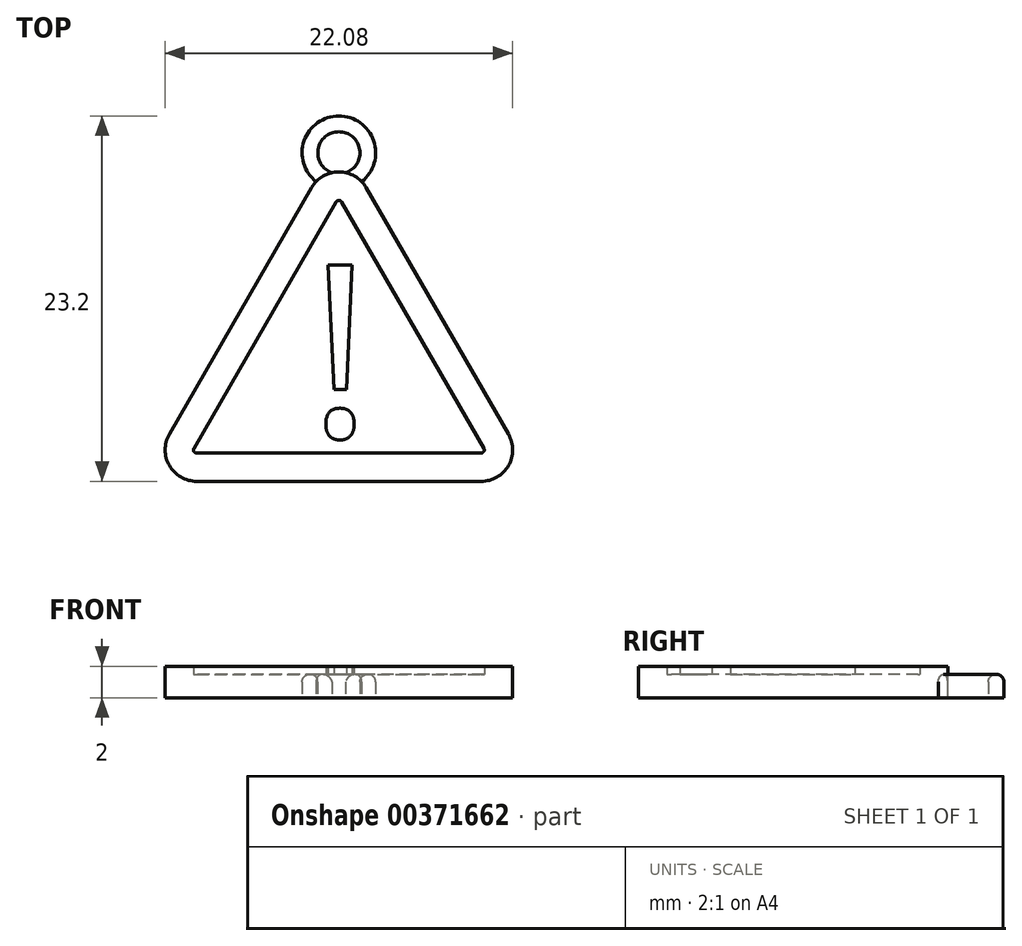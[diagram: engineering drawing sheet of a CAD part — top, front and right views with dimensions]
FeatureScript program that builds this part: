
annotation { "Feature Type Name" : "Feature", "Feature Type Description" : "" }
export const myFeature = defineFeature(function(context is Context, id is Id, definition is map)
    precondition{}
    {
        {
            var Q0;
            Q0=qCreatedBy(makeId("Top.planeOp"),FACE);
            var sketch = newSketch(context, id + "F0", { "sketchPlane" : qUnion([Q0])});
            skLineSegment(sketch, "E0", {"start": v(-12.5, 0) * mm, "end": v(12.5, 0) * mm});
            skLineSegment(sketch, "E1", {"start": v(12.5, 0) * mm, "end": v(0, 21.65) * mm});
            skLineSegment(sketch, "E2", {"start": v(-12.5, 0) * mm, "end": v(0, 21.65) * mm});
            skSolve(sketch);
        }
        {
            var Q0;
            Q0=makeQuery(id+"F0.imprint","IMPRINT",FACE,{"disambiguationData":[TD([[makeQuery(id+"F0.imprint","IMPRINT",EDGE,{"derivedFrom":sQuery(id+"F0.wireOp",EDGE,"E0")}),1.0]])]});
            extrude(context, id + "F1", {"entities" : qUnion([Q0]), "depth" : 1.5 * mm});
        }
        {
            var Q0;
            Q0=makeQuery(id+"F1.opExtrude","SWEPT_EDGE",EDGE,{"disambiguationData":[OSD([sQuery(id+"F0.wireOp",EDGE,"E1"),sQuery(id+"F0.wireOp",EDGE,"E2")])]});
            var Q1;
            Q1=makeQuery(id+"F1.opExtrude","SWEPT_EDGE",EDGE,{"disambiguationData":[OSD([sQuery(id+"F0.wireOp",EDGE,"E0"),sQuery(id+"F0.wireOp",EDGE,"E1")])]});
            var Q2;
            Q2=makeQuery(id+"F1.opExtrude","SWEPT_EDGE",EDGE,{"disambiguationData":[OSD([sQuery(id+"F0.wireOp",EDGE,"E0"),sQuery(id+"F0.wireOp",EDGE,"E2")])]});
            fillet(context, id + "F2", {"entities" : qUnion([Q0, Q1, Q2]), "radius" : 2 * mm, "tangentPropagation" : true, "allowEdgeOverflow" : false});
        }
        {
            var Q0;
            Q0=makeQuery(id+"F1.opExtrude","CAP_FACE",FACE,{"disambiguationData":[OSD([sQuery(id+"F0.wireOp",EDGE,"E0"),sQuery(id+"F0.wireOp",EDGE,"E1"),sQuery(id+"F0.wireOp",EDGE,"E2")])],"isStart":false});
            var sketch = newSketch(context, id + "F3", { "sketchPlane" : qUnion([Q0])});
            skLineSegment(sketch, "E3.0.0", {"start": v(-1.73, 18.65) * mm, "end": v(-10.77, 3) * mm});
            skArc(sketch, "E3.0.1", {"start": v(-10.77, 3) * mm, "mid": v(-10.77, 1) * mm, "end": v(-9.04, 0) * mm});
            skLineSegment(sketch, "E3.0.2", {"start": v(-9.04, 0) * mm, "end": v(9.04, 0) * mm});
            skArc(sketch, "E3.0.3", {"start": v(9.04, 0) * mm, "mid": v(10.77, 1) * mm, "end": v(10.77, 3) * mm});
            skLineSegment(sketch, "E3.0.4", {"start": v(10.77, 3) * mm, "end": v(1.73, 18.65) * mm});
            skArc(sketch, "E3.0.5", {"start": v(1.73, 18.65) * mm, "mid": v(0, 19.65) * mm, "end": v(-1.73, 18.65) * mm});
            skArc(sketch, "E4.0", {"start": v(0.17, 17.75) * mm, "mid": v(0, 17.85) * mm, "end": v(-0.17, 17.75) * mm});
            skArc(sketch, "E4.1", {"start": v(-9.2, 2.1) * mm, "mid": v(-9.2, 1.9) * mm, "end": v(-9.04, 1.8) * mm});
            skLineSegment(sketch, "E4.2", {"start": v(-9.04, 1.8) * mm, "end": v(9.04, 1.8) * mm});
            skLineSegment(sketch, "E4.3", {"start": v(-0.17, 17.75) * mm, "end": v(-9.2, 2.1) * mm});
            skArc(sketch, "E4.4", {"start": v(9.04, 1.8) * mm, "mid": v(9.2, 1.9) * mm, "end": v(9.2, 2.1) * mm});
            skLineSegment(sketch, "E4.5", {"start": v(9.2, 2.1) * mm, "end": v(0.17, 17.75) * mm});
            skText(sketch, "E5", { "text": "!", "fontName": "OpenSans-Regular.ttf"});
            const initialGuessF3  = {"E5": [-0.00196, 0.00284, 1, 0, 0.011]};
            skSetInitialGuess(sketch, initialGuessF3);
            skSolve(sketch);
        }
        {
            var Q0;
            Q0=makeQuery(id+"F3.imprint","IMPRINT",FACE,{"disambiguationData":[TD([[makeQuery(id+"F3.imprint","IMPRINT",EDGE,{"derivedFrom":sQuery(id+"F3.wireOp",EDGE,"E3.0.0")}),-1.0]])]});
            var Q1;
            Q1=makeQuery(id+"F3.imprint","IMPRINT",FACE,{"disambiguationData":[TD([[makeQuery(id+"F3.imprint","IMPRINT",EDGE,{"derivedFrom":sQuery(id+"F3.wireOp",EDGE,"E5.sketch_text.stroke-0")}),-1.0]])]});
            var Q2;
            Q2 = qSketchRegion(id + "F3", true);
            var Q3;
            Q3=makeQuery(id+"F3.imprint","IMPRINT",FACE,{"disambiguationData":[TD([[makeQuery(id+"F3.imprint","IMPRINT",EDGE,{"derivedFrom":sQuery(id+"F3.wireOp",EDGE,"E5.sketch_text.stroke-4")}),-1.0]])]});
            extrude(context, id + "F4", {"entities" : qUnion([Q0, Q1, Q2, Q3]), "operationType" : NewBodyOperationType.ADD, "depth" : 0.5 * mm});
        }
        {
            var Q0;
            Q0=makeQuery(id+"F1.opExtrude","CAP_FACE",FACE,{"disambiguationData":[OSD([sQuery(id+"F0.wireOp",EDGE,"E0"),sQuery(id+"F0.wireOp",EDGE,"E1"),sQuery(id+"F0.wireOp",EDGE,"E2")])],"isStart":true});
            var sketch = newSketch(context, id + "F5", { "sketchPlane" : qUnion([Q0])});
            skCircle(sketch, "E6", {"center": v(0, -20.87) * mm, "radius": 2.34 * mm});
            skPoint(sketch, "E6.centerSnap0", {"position": v(0, -19.65) * mm});
            skCircle(sketch, "E7", {"center": v(0, -20.87) * mm, "radius": 1.34 * mm});
            skSolve(sketch);
        }
        {
            var Q0;
            {var subQ0=sQuery(id+"F5.wireOp",EDGE,"E6");var subQ1=sQuery(id+"F0.wireOp",EDGE,"E2");var subQ2=sQuery(id+"F0.wireOp",EDGE,"E1");var subQ3=makeQuery(id+"F2.opFillet","BLEND_EDGE",EDGE,{"blendedFrom":[makeQuery(id+"F1.opExtrude","SWEPT_EDGE",EDGE,{"disambiguationData":[OSD([subQ2,subQ1])]}),makeQuery(id+"F1.opExtrude","CAP_FACE",FACE,{"disambiguationData":[OSD([sQuery(id+"F0.wireOp",EDGE,"E0"),subQ2,subQ1])],"isStart":true})],"blendedInto":[makeQuery(id+"F1.opExtrude","CAP_FACE",FACE,{"disambiguationData":[OSD([sQuery(id+"F0.wireOp",EDGE,"E0"),subQ2,subQ1])],"isStart":true})]});var subQ4=makeQuery(id+"F5.imprint","INTERSECT",VERTEX,{"disambiguationData":[OD(0.0)],"derivedFrom":[subQ3,subQ0]});Q0=makeQuery(id+"F5.imprint","IMPRINT",FACE,{"disambiguationData":[TD([[makeQuery(id+"F5.imprint","IMPRINT",EDGE,{"disambiguationData":[TD([[subQ4,1.0]])],"derivedFrom":subQ0}),1.0]])]});}
            extrude(context, id + "F6", {"entities" : qUnion([Q0]), "operationType" : NewBodyOperationType.ADD, "oppositeDirection" : true, "depth" : 1.5 * mm});
        }
        {
            var Q0;
            Q0=makeQuery(id+"F6.opExtrude","CAP_EDGE",EDGE,{"disambiguationData":[OSD([sQuery(id+"F5.wireOp",EDGE,"E6")])],"isStart":false});
            var Q1;
            Q1=makeQuery(id+"F6.opExtrude","CAP_EDGE",EDGE,{"disambiguationData":[OSD([sQuery(id+"F5.wireOp",EDGE,"E7")])],"isStart":false});
            fillet(context, id + "F7", {"entities" : qUnion([Q0, Q1]), "radius" : 0.5 * mm, "tangentPropagation" : true, "allowEdgeOverflow" : false});
        }
    });
